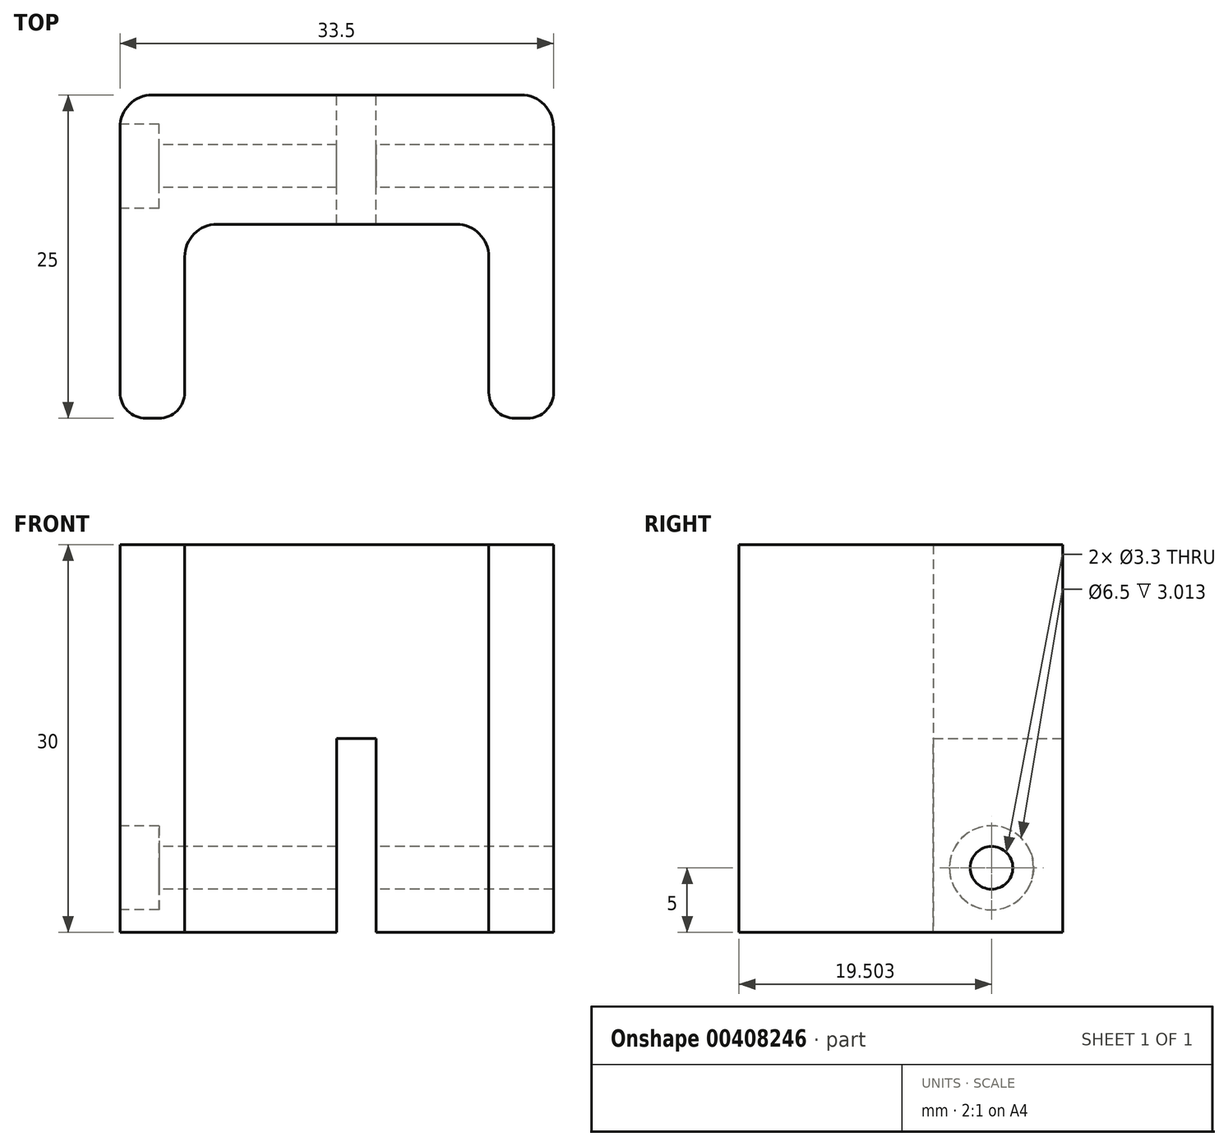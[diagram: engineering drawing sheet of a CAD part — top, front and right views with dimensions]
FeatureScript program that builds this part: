
annotation { "Feature Type Name" : "Feature", "Feature Type Description" : "" }
export const myFeature = defineFeature(function(context is Context, id is Id, definition is map)
    precondition{}
    {
        {
            var Q0;
            Q0=qCreatedBy(makeId("Top.planeOp"),FACE);
            var sketch = newSketch(context, id + "F0", { "sketchPlane" : qUnion([Q0])});
            skLineSegment(sketch, "E0", {"start": v(-9.26, -11.84) * mm, "end": v(-8.26, -11.84) * mm});
            skLineSegment(sketch, "E1", {"start": v(-6.26, -9.84) * mm, "end": v(-6.26, 0.66) * mm});
            skLineSegment(sketch, "E2", {"start": v(-3.76, 3.16) * mm, "end": v(14.74, 3.16) * mm});
            skLineSegment(sketch, "E3", {"start": v(17.24, 0.66) * mm, "end": v(17.24, -9.84) * mm});
            skLineSegment(sketch, "E4", {"start": v(19.24, -11.84) * mm, "end": v(20.24, -11.84) * mm});
            skLineSegment(sketch, "E5", {"start": v(22.24, -9.84) * mm, "end": v(22.24, 10.66) * mm});
            skLineSegment(sketch, "E6", {"start": v(19.74, 13.16) * mm, "end": v(-8.76, 13.16) * mm});
            skLineSegment(sketch, "E7", {"start": v(-11.26, 10.66) * mm, "end": v(-11.26, -9.84) * mm});
            skPoint(sketch, "E8.visualSharp", {"position": v(-11.26, 13.16) * mm});
            skArc(sketch, "E8.filletArc", {"start": v(-8.76, 13.16) * mm, "mid": v(-10.52, 12.43) * mm, "end": v(-11.26, 10.66) * mm});
            skPoint(sketch, "E9.visualSharp", {"position": v(22.24, 13.16) * mm});
            skArc(sketch, "E9.filletArc", {"start": v(22.24, 10.66) * mm, "mid": v(21.51, 12.43) * mm, "end": v(19.74, 13.16) * mm});
            skPoint(sketch, "E10.visualSharp", {"position": v(-6.26, 3.16) * mm});
            skArc(sketch, "E10.filletArc", {"start": v(-3.76, 3.16) * mm, "mid": v(-5.52, 2.43) * mm, "end": v(-6.26, 0.66) * mm});
            skPoint(sketch, "E11.visualSharp", {"position": v(17.24, 3.16) * mm});
            skArc(sketch, "E11.filletArc", {"start": v(17.24, 0.66) * mm, "mid": v(16.51, 2.43) * mm, "end": v(14.74, 3.16) * mm});
            skPoint(sketch, "E12.visualSharp", {"position": v(-11.26, -11.84) * mm});
            skArc(sketch, "E12.filletArc", {"start": v(-11.26, -9.84) * mm, "mid": v(-10.67, -11.25) * mm, "end": v(-9.26, -11.84) * mm});
            skPoint(sketch, "E13.visualSharp", {"position": v(17.24, -11.84) * mm});
            skArc(sketch, "E13.filletArc", {"start": v(17.24, -9.84) * mm, "mid": v(17.83, -11.25) * mm, "end": v(19.24, -11.84) * mm});
            skPoint(sketch, "E14.visualSharp", {"position": v(22.24, -11.84) * mm});
            skArc(sketch, "E14.filletArc", {"start": v(20.24, -11.84) * mm, "mid": v(21.66, -11.25) * mm, "end": v(22.24, -9.84) * mm});
            skPoint(sketch, "E15.visualSharp", {"position": v(-6.26, -11.84) * mm});
            skArc(sketch, "E15.filletArc", {"start": v(-8.26, -11.84) * mm, "mid": v(-6.84, -11.25) * mm, "end": v(-6.26, -9.84) * mm});
            skSolve(sketch);
        }
        {
            var Q0;
            Q0=makeQuery(id+"F0.imprint","IMPRINT",FACE,{"disambiguationData":[TD([[makeQuery(id+"F0.imprint","IMPRINT",EDGE,{"derivedFrom":sQuery(id+"F0.wireOp",EDGE,"E0")}),1.0]])]});
            extrude(context, id + "F1", {"entities" : qUnion([Q0]), "depth" : 30 * mm});
        }
        {
            var Q0;
            Q0=makeQuery(id+"F1.opExtrude","SWEPT_FACE",FACE,{"disambiguationData":[OSD([sQuery(id+"F0.wireOp",EDGE,"E6")])]});
            var sketch = newSketch(context, id + "F2", { "sketchPlane" : qUnion([Q0])});
            skLineSegment(sketch, "E16", {"start": v(-5.5, 0) * mm, "end": v(-5.5, 15) * mm});
            skLineSegment(sketch, "E17", {"start": v(-5.5, 15) * mm, "end": v(-8.54, 15) * mm});
            skLineSegment(sketch, "E18", {"start": v(-8.54, 15) * mm, "end": v(-8.54, 0) * mm});
            skLineSegment(sketch, "E19", {"start": v(-8.54, 0) * mm, "end": v(-5.5, 0) * mm});
            skSolve(sketch);
        }
        {
            var Q0;
            Q0 = qSketchRegion(id + "F2", true);
            extrude(context, id + "F3", {"entities" : qUnion([Q0]), "operationType" : NewBodyOperationType.REMOVE, "endBound" : BoundingType.THROUGH_ALL, "oppositeDirection" : true, "depth" : 25 * mm});
        }
        {
            var Q0;
            Q0=makeQuery(id+"F1.opExtrude","SWEPT_FACE",FACE,{"disambiguationData":[OSD([sQuery(id+"F0.wireOp",EDGE,"E7")])]});
            var sketch = newSketch(context, id + "F4", { "sketchPlane" : qUnion([Q0])});
            skPoint(sketch, "E20", {"position": v(-7.66, 5) * mm});
            skSolve(sketch);
        }
        {
            var Q0;
            Q0=sQuery(id+"F4.wireOp",VERTEX,"E20");
            var Q1;
            Q1=makeQuery(id+"F1.opExtrude","SWEPT_BODY",BODY,{"disambiguationData":[OSD([sQuery(id+"F0.wireOp",EDGE,"E0"),sQuery(id+"F0.wireOp",EDGE,"E1"),sQuery(id+"F0.wireOp",EDGE,"E2"),sQuery(id+"F0.wireOp",EDGE,"E3"),sQuery(id+"F0.wireOp",EDGE,"E4"),sQuery(id+"F0.wireOp",EDGE,"E5"),sQuery(id+"F0.wireOp",EDGE,"E6"),sQuery(id+"F0.wireOp",EDGE,"E7"),sQuery(id+"F0.wireOp",EDGE,"E8.filletArc"),sQuery(id+"F0.wireOp",EDGE,"E9.filletArc"),sQuery(id+"F0.wireOp",EDGE,"E10.filletArc"),sQuery(id+"F0.wireOp",EDGE,"E11.filletArc"),sQuery(id+"F0.wireOp",EDGE,"E12.filletArc"),sQuery(id+"F0.wireOp",EDGE,"E13.filletArc"),sQuery(id+"F0.wireOp",EDGE,"E14.filletArc"),sQuery(id+"F0.wireOp",EDGE,"E15.filletArc")])]});
            hole(context, id + "F5", {"style" : HoleStyle.C_BORE, "endStyle" : HoleEndStyle.THROUGH, "standardTappedOrClearance" : lookupTablePath({ "standard" : "ISO", "fit" : "Normal", "size" : "M3", "type" : "Clearance" }), "standardBlindInLast" : lookupTablePath({ "fit" : "Standard", "standard" : "ISO", "size" : "M3", "type" : "Clearance" }), "holeDiameter" : 3.3 * mm, "cBoreDiameter" : 6.5 * mm, "cBoreDepth" : 3 * mm, "isTappedThrough" : true, "tappedDepth" : 12 * mm, "tapClearance" : 3, "locations" : qUnion([Q0]), "scope" : qUnion([Q1])});
        }
    });
